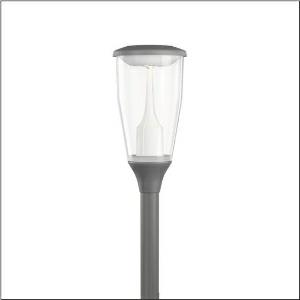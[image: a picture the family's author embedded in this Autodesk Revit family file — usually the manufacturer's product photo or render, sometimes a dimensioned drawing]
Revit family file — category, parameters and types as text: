
# Revit family: dl_11_iq___st1_2a_5xa5565af14h000022_cb01
name_source: partatom
category: Lighting Fixtures
units: mm (PartAtom-declared; Revit-internal decimal feet)

## family parameters
Cut with Voids When Loaded = No
Host = Face
Light Source = No
Part Type = Normal
Room Calculation Point = No
Round Connector Dimension = Use Diameter
Shared = No

## types (1)
- --- (1 x LED, 1560 lm, 12.9 W, 2200K)
    Apparent Load = 13 VA
    CIE Flux Codes = 24 63 94 96 100
    Color Rendering = 70
    Color Temperature = 2200K
    Default Elevation = 1800 mm
    Description = DL 11 iQ, mast luminaire, Module 540 iQ-SR, primary light control with 3 zone facetted reflector, of plastic, silver coated, highly specular, structured, primary optical cover: cover, of PMMA, transparent, light distribution: ST1.2a, light emission: direct distribution, primary light characteristic: asymmetric, installation type: post-top, LED, High Power LED, rated luminous flux: 1.560lm, luminous efficacy: 149lm/W, light colour: 722, colour temperature: 2200K, control gear: iQ Street-Remote, control: Street-Remote, Auto-Match, Temp-Guard, Lumen-Switch, Night-Set, Smart-Wire, Light-Fading, Desk-Remote (wireless, voltage-free reading and setting of iQ features in the workshop via application-optimized NFC function/RFID function), optimised constant luminous flux control (CLO 2.0), mains connection: 220..240V, AC, 50/60Hz, connection cable pre-assembled, cable length: 5,5m, start of lifetime: 13W, end of service life: 13W, reduction: 5W, luminaire housing, upper part, of diecast aluminium, coated, SITECO metallic grey (DB 702S), spigot size: 60mm (post-top), mounting height: 3..5m, post-top mast mounting element, of diecast aluminium, coated, SITECO metallic grey (DB 702S), Module 540 iQ-SR, traffic white (RAL 9016), equipment: standard, protection rating (complete): IP66, insulation class (complete): insulation class II (safety insulation), certification: CE, ENEC, ENEC+, VDE, impact resistance: IK07, packaging unit: 1 piece

Light Distribution: ST1.2a
    Height = 665 mm
    Lamp = 1 x LED
    Lamp Light Flux = 1560 lm
    Lamp Power = 12.9 W
    Lamp count = 1
    Length = 334 mm
    Luminous efficacy = 121 lm/W
    Manufacturer = Siteco
    ModVariant = No
    Model = 5XA5565AF14H000022
    Number of Poles = 1
    OnlyDefault = Yes
    Power Factor = 1
    Product Name = DL 11 iQ | ST1.2a
    Product group = mast luminaire | pylon top
    ProductGroupID = 6100
    Protection Class = Protection class II
    Protection Degree = IP 66
    RLX_Detail_Level = 1
    RLX_Emergency_Light_Flux = 0 lm
    RLX_Emergency_Type = 0
    RLX_Emergency_Type_DB = No
    RlxData = <blob elided: 155005 chars, md5=14d55ee7>
    Socket = socket
    Standby Power = 0 W
    System Light Flux = 1560 lm
    System Power = 13 W
    Type Comments = factory setting: luminous flux: 100 % | dim-lin: 254 | 516 mA
    Type Image = l_1258354.jpg
    URL = http://relux.com
    VarID = @adj_099129
    Voltage = 0 V
    Weight = 0.00 kg
    Width = 0 mm  [stored 0 ft]

note: [stored X ft] marks values corroborated as IEEE doubles in the binary element streams (Revit-internal decimal feet)

## geometry (parser evidence)
native form markers: Blend x4, Sweep x11
no freeform markers — native parametric forms only
